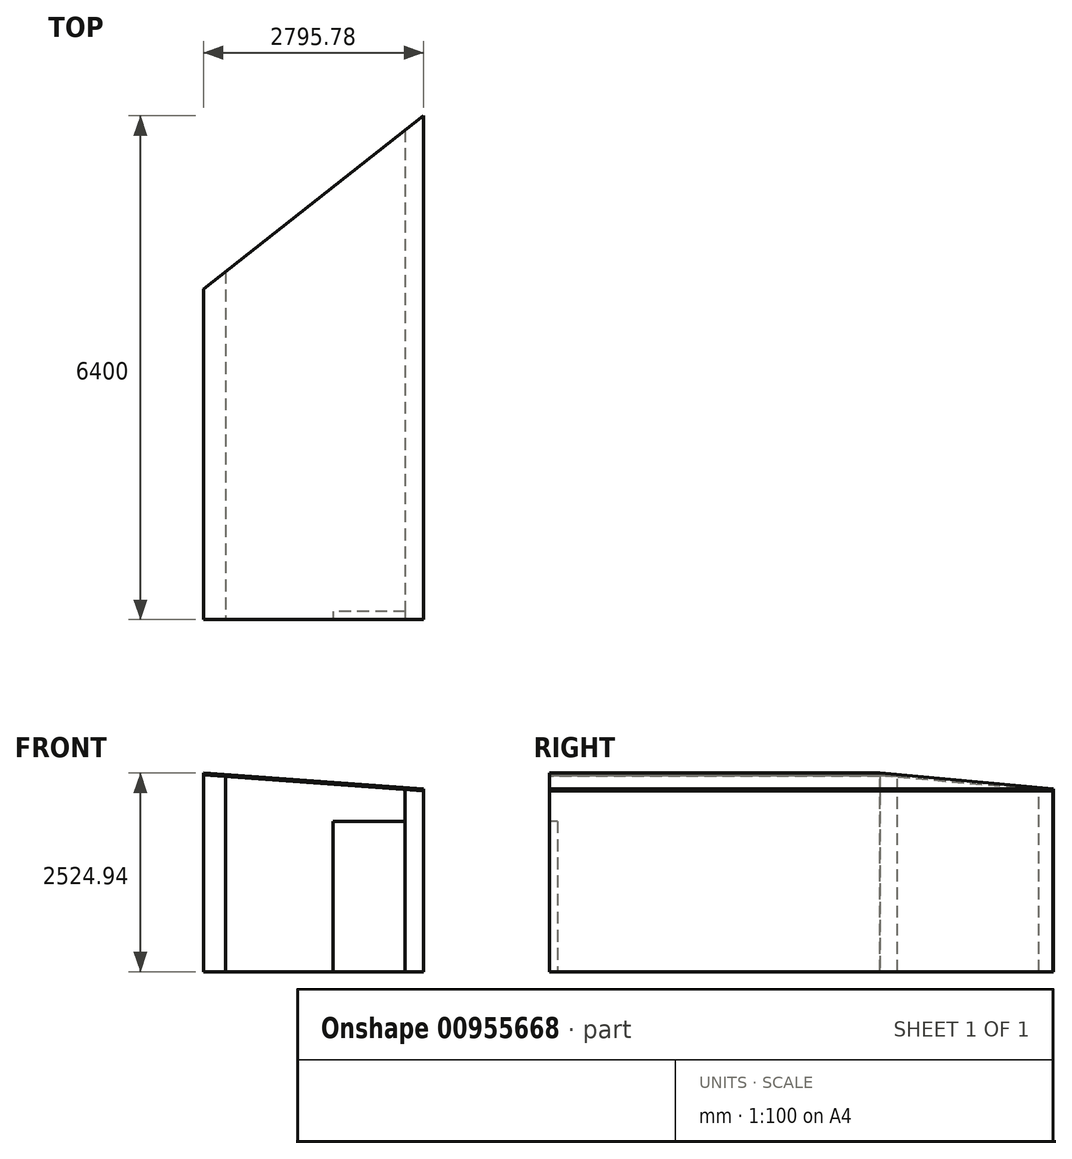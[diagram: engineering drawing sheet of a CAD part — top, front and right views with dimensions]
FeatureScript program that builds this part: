
annotation { "Feature Type Name" : "Feature", "Feature Type Description" : "" }
export const myFeature = defineFeature(function(context is Context, id is Id, definition is map)
    precondition{}
    {
        {
            var Q0;
            Q0=qCreatedBy(makeId("Front.planeOp"),FACE);
            var sketch = newSketch(context, id + "F0", { "sketchPlane" : qUnion([Q0])});
            skLineSegment(sketch, "E0", {"start": v(0, 0) * mm, "end": v(0, 2300) * mm});
            skPoint(sketch, "E1.end.orphan", {"position": v(-1397, 0) * mm});
            skPoint(sketch, "E2.end.orphan", {"position": v(1397, 0) * mm});
            skLineSegment(sketch, "E3.bottom", {"start": v(-1397, 0) * mm, "end": v(1397, 0) * mm});
            skLineSegment(sketch, "E3.top", {"start": v(-1397, 2300) * mm, "end": v(1397, 2300) * mm});
            skLineSegment(sketch, "E3.left", {"start": v(-1397, 0) * mm, "end": v(-1397, 2300) * mm});
            skLineSegment(sketch, "E3.right", {"start": v(1397, 0) * mm, "end": v(1397, 2300) * mm});
            skSolve(sketch);
        }
        {
            var Q0;
            Q0 = qSketchRegion(id + "F0", true);
            extrude(context, id + "F1", {"entities" : qUnion([Q0]), "oppositeDirection" : true, "depth" : 6400 * mm, "offsetDistance" : 25 * mm});
        }
        {
            var Q0;
            Q0=makeQuery(id+"F1.opExtrude","CAP_FACE",FACE,{"disambiguationData":[OSD([sQuery(id+"F0.wireOp",EDGE,"E3.bottom"),sQuery(id+"F0.wireOp",EDGE,"E3.top"),sQuery(id+"F0.wireOp",EDGE,"E3.left"),sQuery(id+"F0.wireOp",EDGE,"E3.right")])],"isStart":false});
            var sketch = newSketch(context, id + "F2", { "sketchPlane" : qUnion([Q0])});
            skLineSegment(sketch, "E4", {"start": v(1397, 2300) * mm, "end": v(1397, 2500) * mm});
            skLineSegment(sketch, "E5", {"start": v(1397, 2500) * mm, "end": v(-1397, 2300) * mm});
            skSolve(sketch);
        }
        {
            var Q0;
            Q0=makeQuery(id+"F2.imprint","IMPRINT",FACE,{"disambiguationData":[TD([[makeQuery(id+"F2.imprint","IMPRINT",EDGE,{"derivedFrom":sQuery(id+"F2.wireOp",EDGE,"E4")}),1.0]])]});
            var Q1;
            Q1=makeQuery(id+"F1.opExtrude","CAP_FACE",FACE,{"disambiguationData":[OSD([sQuery(id+"F0.wireOp",EDGE,"E3.bottom"),sQuery(id+"F0.wireOp",EDGE,"E3.top"),sQuery(id+"F0.wireOp",EDGE,"E3.left"),sQuery(id+"F0.wireOp",EDGE,"E3.right")])],"isStart":true});
            extrude(context, id + "F3", {"entities" : qUnion([Q0]), "operationType" : NewBodyOperationType.ADD, "endBound" : BoundingType.UP_TO_SURFACE, "oppositeDirection" : true, "depth" : 6380 * mm, "endBoundEntityFace" : qUnion([Q1]), "offsetDistance" : 25 * mm});
        }
        {
            var Q0;
            Q0=makeQuery(id+"F1.opExtrude","SWEPT_FACE",FACE,{"disambiguationData":[OSD([sQuery(id+"F0.wireOp",EDGE,"E3.bottom")])]});
            var sketch = newSketch(context, id + "F4", { "sketchPlane" : qUnion([Q0])});
            skPoint(sketch, "E6", {"position": v(1397, -4200) * mm});
            skLineSegment(sketch, "E7", {"start": v(1397, -4200) * mm, "end": v(-1397, -4200) * mm});
            skLineSegment(sketch, "E8", {"start": v(-1397, -4200) * mm, "end": v(1397, -6400) * mm});
            skSolve(sketch);
        }
        {
            var Q0;
            {var subQ0=sQuery(id+"F4.wireOp",EDGE,"E8");Q0=makeQuery(id+"F4.imprint","IMPRINT",FACE,{"disambiguationData":[TD([[makeQuery(id+"F4.imprint","IMPRINT",EDGE,{"derivedFrom":subQ0}),-1.0]])]});}
            var Q1;
            Q1=makeQuery(id+"F3.opExtrude","SWEPT_FACE",FACE,{"disambiguationData":[OSD([sQuery(id+"F2.wireOp",EDGE,"E5")])]});
            extrude(context, id + "F5", {"entities" : qUnion([Q0]), "operationType" : NewBodyOperationType.REMOVE, "endBound" : BoundingType.UP_TO_SURFACE, "oppositeDirection" : true, "depth" : 25 * mm, "endBoundEntityFace" : qUnion([Q1]), "offsetDistance" : 25 * mm});
        }
        {
            var Q0;
            Q0=makeQuery(id+"F1.opExtrude","SWEPT_FACE",FACE,{"disambiguationData":[OSD([sQuery(id+"F0.wireOp",EDGE,"E3.bottom")])]});
            shell(context, id + "F6", {"entities" : qUnion([Q0]), "thickness" : 2.5 * mm});
        }
        {
            var Q0;
            {var subQ0=sQuery(id+"F0.wireOp",EDGE,"E3.top");Q0=makeQuery(id+"F3.boolean.opBoolean","MERGE",FACE,{"derivedFrom":[makeQuery(id+"F1.opExtrude","CAP_FACE",FACE,{"disambiguationData":[OSD([sQuery(id+"F0.wireOp",EDGE,"E3.bottom"),subQ0,sQuery(id+"F0.wireOp",EDGE,"E3.left"),sQuery(id+"F0.wireOp",EDGE,"E3.right")])],"isStart":true}),makeQuery(id+"F3.opExtrude","CAP_FACE",FACE,{"disambiguationData":[OSD([subQ0,sQuery(id+"F2.wireOp",EDGE,"E4"),sQuery(id+"F2.wireOp",EDGE,"E5")])],"isStart":false})]});}
            var sketch = newSketch(context, id + "F7", { "sketchPlane" : qUnion([Q0])});
            skLineSegment(sketch, "E9.left", {"start": v(-1114.76, 0) * mm, "end": v(-1114.76, 1912) * mm});
            skLineSegment(sketch, "E10.left", {"start": v(1167, 1912) * mm, "end": v(1167, 0) * mm});
            skLineSegment(sketch, "E10.right", {"start": v(252.6, 1912) * mm, "end": v(252.6, 0) * mm});
            skPoint(sketch, "E11", {"position": v(1167, 1912) * mm});
            skLineSegment(sketch, "E12", {"start": v(1167, 1912) * mm, "end": v(-1114.76, 1912) * mm});
            skLineSegment(sketch, "E13", {"start": v(1167, 1912) * mm, "end": v(1167, 2316.46) * mm});
            skLineSegment(sketch, "E14", {"start": v(-1114.76, 1912) * mm, "end": v(-1114.76, 2479.8) * mm});
            skSolve(sketch);
        }
        {
            var Q0;
            Q0=makeQuery(id+"F3.opExtrude","SWEPT_FACE",FACE,{"disambiguationData":[OSD([sQuery(id+"F2.wireOp",EDGE,"E5")])]});
            var sketch = newSketch(context, id + "F8", { "sketchPlane" : qUnion([Q0])});
            skSolve(sketch);
        }
        {
            var Q0;
            Q0 = qSketchRegion(id + "F8", true);
            var Q1;
            {var subQ0=sQuery(id+"F2.wireOp",EDGE,"E5");Q1=makeQuery(id+"F8.imprint","IMPRINT",FACE,{"disambiguationData":[TD([[makeQuery(id+"F8.imprint","IMPRINT",EDGE,{"derivedFrom":makeQuery(id+"F3.opExtrude","CAP_EDGE",EDGE,{"disambiguationData":[OSD([subQ0])],"isStart":false})}),1.0]])]});}
            extrude(context, id + "F9", {"entities" : qUnion([Q0, Q1]), "depth" : 25 * mm, "offsetDistance" : 25 * mm});
        }
        {
            var Q0;
            {var subQ2=sQuery(id+"F7.wireOp",EDGE,"E10.left");Q0=makeQuery(id+"F7.imprint","IMPRINT",FACE,{"disambiguationData":[TD([[makeQuery(id+"F7.imprint","IMPRINT",EDGE,{"derivedFrom":subQ2}),1.0]])]});}
            var Q1;
            Q1=makeQuery(id+"F6.opShell","OFFSET_FACE",FACE,{"disambiguationData":[OSD([sQuery(id+"F4.wireOp",EDGE,"E8")])]});
            extrude(context, id + "F10", {"entities" : qUnion([Q0]), "endBound" : BoundingType.UP_TO_SURFACE, "oppositeDirection" : true, "depth" : 25 * mm, "endBoundEntityFace" : qUnion([Q1]), "offsetDistance" : 25 * mm});
        }
        {
            var Q0;
            {var subQ2=sQuery(id+"F7.wireOp",EDGE,"E9.left");Q0=makeQuery(id+"F7.imprint","IMPRINT",FACE,{"disambiguationData":[TD([[makeQuery(id+"F7.imprint","IMPRINT",EDGE,{"derivedFrom":subQ2}),1.0]])]});}
            var Q1;
            Q1=makeQuery(id+"F6.opShell","OFFSET_FACE",FACE,{"disambiguationData":[OSD([sQuery(id+"F4.wireOp",EDGE,"E8")])]});
            extrude(context, id + "F11", {"entities" : qUnion([Q0]), "endBound" : BoundingType.UP_TO_SURFACE, "oppositeDirection" : true, "depth" : 25 * mm, "endBoundEntityFace" : qUnion([Q1]), "offsetDistance" : 25 * mm});
        }
        {
            var Q0;
            {var subQ0=sQuery(id+"F7.wireOp",EDGE,"E10.left");Q0=makeQuery(id+"F7.imprint","IMPRINT",FACE,{"disambiguationData":[TD([[makeQuery(id+"F7.imprint","IMPRINT",EDGE,{"derivedFrom":subQ0}),-1.0]])]});}
            extrude(context, id + "F12", {"entities" : qUnion([Q0]), "oppositeDirection" : true, "depth" : 100 * mm, "offsetDistance" : 25 * mm});
        }
    });
